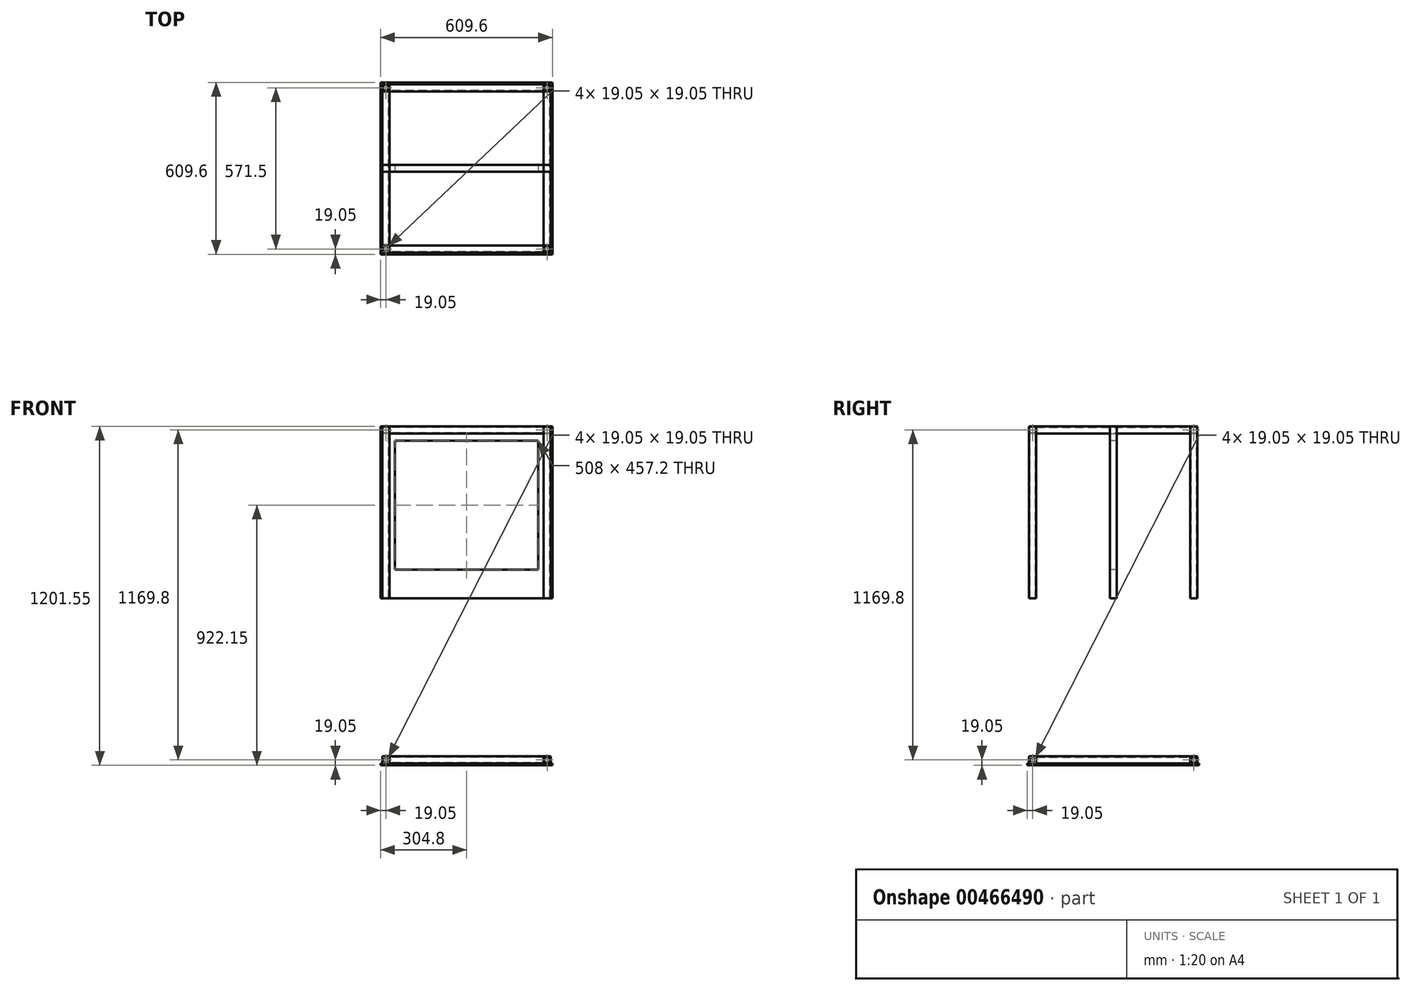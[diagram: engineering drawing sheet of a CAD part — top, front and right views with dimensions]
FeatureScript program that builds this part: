
annotation { "Feature Type Name" : "Feature", "Feature Type Description" : "" }
export const myFeature = defineFeature(function(context is Context, id is Id, definition is map)
    precondition{}
    {
        {
            assignVariable(context, id + "F0", {"name" : "OH", "anyValue" : 24});
        }
        {
            assignVariable(context, id + "F1", {"name" : "OD", "anyValue" : 24});
        }
        {
            var Q0;
            Q0=qCreatedBy(makeId("Front.planeOp"),FACE);
            var sketch = newSketch(context, id + "F2", { "sketchPlane" : qUnion([Q0])});
            skLineSegment(sketch, "E0.bottom", {"start": v(-304.8, 0) * mm, "end": v(304.8, 0) * mm});
            skLineSegment(sketch, "E0.top", {"start": v(-304.8, 609.6) * mm, "end": v(304.8, 609.6) * mm});
            skLineSegment(sketch, "E0.left", {"start": v(-304.8, 0) * mm, "end": v(-304.8, 609.6) * mm});
            skLineSegment(sketch, "E0.right", {"start": v(304.8, 0) * mm, "end": v(304.8, 609.6) * mm});
            skSolve(sketch);
        }
        {
            var Q0;
            Q0 = qSketchRegion(id + "F2", true);
            extrude(context, id + "F3", {"entities" : qUnion([Q0]), "depth" : (getVariable(context, 'OD') / 2) * mm, "hasSecondDirection" : true, "secondDirectionOppositeDirection" : true, "secondDirectionDepth" : (getVariable(context, 'OD') / 2) * mm});
        }
        {
            var Q0;
            Q0=makeQuery(id+"F3.opExtrude","CAP_FACE",FACE,{"disambiguationData":[OSD([sQuery(id+"F2.wireOp",EDGE,"E0.bottom"),sQuery(id+"F2.wireOp",EDGE,"E0.top"),sQuery(id+"F2.wireOp",EDGE,"E0.left"),sQuery(id+"F2.wireOp",EDGE,"E0.right")])],"isStart":false});
            var sketch = newSketch(context, id + "F4", { "sketchPlane" : qUnion([Q0])});
            skLineSegment(sketch, "E1.bottom", {"start": v(-254, 101.6) * mm, "end": v(254, 101.6) * mm});
            skLineSegment(sketch, "E1.top", {"start": v(-254, 558.8) * mm, "end": v(254, 558.8) * mm});
            skLineSegment(sketch, "E1.left", {"start": v(-254, 101.6) * mm, "end": v(-254, 558.8) * mm});
            skLineSegment(sketch, "E1.right", {"start": v(254, 101.6) * mm, "end": v(254, 558.8) * mm});
            skSolve(sketch);
        }
        {
            var Q0;
            Q0=makeQuery(id+"F3.opExtrude","SWEPT_FACE",FACE,{"disambiguationData":[OSD([sQuery(id+"F2.wireOp",EDGE,"E0.top")])]});
            var sketch = newSketch(context, id + "F5", { "sketchPlane" : qUnion([Q0])});
            skLineSegment(sketch, "E2.bottom", {"start": v(-298.45, 298.45) * mm, "end": v(298.45, 298.45) * mm});
            skLineSegment(sketch, "E2.top", {"start": v(-298.45, -298.45) * mm, "end": v(298.45, -298.45) * mm});
            skLineSegment(sketch, "E2.left", {"start": v(-298.45, 298.45) * mm, "end": v(-298.45, -298.45) * mm});
            skLineSegment(sketch, "E2.right", {"start": v(298.45, 298.45) * mm, "end": v(298.45, -298.45) * mm});
            skSolve(sketch);
        }
        {
            var Q0;
            Q0=makeQuery(id+"F5.imprint","IMPRINT",FACE,{"disambiguationData":[TD([[makeQuery(id+"F5.imprint","IMPRINT",EDGE,{"derivedFrom":sQuery(id+"F5.wireOp",EDGE,"E2.bottom")}),-1.0]])]});
            extrude(context, id + "F6", {"entities" : qUnion([Q0]), "operationType" : NewBodyOperationType.REMOVE, "endBound" : BoundingType.THROUGH_ALL, "oppositeDirection" : true, "depth" : 25.4 * mm});
        }
        {
            var Q0;
            Q0=makeQuery(id+"F4.imprint","IMPRINT",FACE,{"disambiguationData":[TD([[makeQuery(id+"F4.imprint","IMPRINT",EDGE,{"derivedFrom":sQuery(id+"F4.wireOp",EDGE,"E1.bottom")}),1.0]])]});
            extrude(context, id + "F7", {"entities" : qUnion([Q0]), "operationType" : NewBodyOperationType.REMOVE, "oppositeDirection" : true, "depth" : 25.4 * mm});
        }
        {
            var Q0;
            Q0=makeQuery(id+"F3.opExtrude","SWEPT_FACE",FACE,{"disambiguationData":[OSD([sQuery(id+"F2.wireOp",EDGE,"E0.top")])]});
            var sketch = newSketch(context, id + "F8", { "sketchPlane" : qUnion([Q0])});
            skLineSegment(sketch, "E3.bottom", {"start": v(-298.45, 298.45) * mm, "end": v(-273.05, 298.45) * mm});
            skLineSegment(sketch, "E3.top", {"start": v(-298.45, 273.05) * mm, "end": v(-273.05, 273.05) * mm});
            skLineSegment(sketch, "E3.left", {"start": v(-298.45, 298.45) * mm, "end": v(-298.45, 273.05) * mm});
            skLineSegment(sketch, "E3.right", {"start": v(-273.05, 298.45) * mm, "end": v(-273.05, 273.05) * mm});
            skLineSegment(sketch, "E4.bottom", {"start": v(-298.45, -298.45) * mm, "end": v(-273.05, -298.45) * mm});
            skLineSegment(sketch, "E4.top", {"start": v(-298.45, -273.05) * mm, "end": v(-273.05, -273.05) * mm});
            skLineSegment(sketch, "E4.left", {"start": v(-298.45, -298.45) * mm, "end": v(-298.45, -273.05) * mm});
            skLineSegment(sketch, "E4.right", {"start": v(-273.05, -298.45) * mm, "end": v(-273.05, -273.05) * mm});
            skLineSegment(sketch, "E5.bottom", {"start": v(298.45, 298.45) * mm, "end": v(273.05, 298.45) * mm});
            skLineSegment(sketch, "E5.top", {"start": v(298.45, 273.05) * mm, "end": v(273.05, 273.05) * mm});
            skLineSegment(sketch, "E5.left", {"start": v(298.45, 298.45) * mm, "end": v(298.45, 273.05) * mm});
            skLineSegment(sketch, "E5.right", {"start": v(273.05, 298.45) * mm, "end": v(273.05, 273.05) * mm});
            skLineSegment(sketch, "E6.bottom", {"start": v(298.45, -298.45) * mm, "end": v(273.05, -298.45) * mm});
            skLineSegment(sketch, "E6.top", {"start": v(298.45, -273.05) * mm, "end": v(273.05, -273.05) * mm});
            skLineSegment(sketch, "E6.left", {"start": v(298.45, -298.45) * mm, "end": v(298.45, -273.05) * mm});
            skLineSegment(sketch, "E6.right", {"start": v(273.05, -298.45) * mm, "end": v(273.05, -273.05) * mm});
            skLineSegment(sketch, "E7.bottom", {"start": v(276.22, -276.23) * mm, "end": v(295.27, -276.23) * mm});
            skLineSegment(sketch, "E7.top", {"start": v(276.22, -295.28) * mm, "end": v(295.27, -295.28) * mm});
            skLineSegment(sketch, "E7.left", {"start": v(276.22, -276.23) * mm, "end": v(276.22, -295.28) * mm});
            skLineSegment(sketch, "E7.right", {"start": v(295.27, -276.23) * mm, "end": v(295.27, -295.28) * mm});
            skLineSegment(sketch, "E8", {"start": v(-298.45, 0) * mm, "end": v(298.45, 0) * mm, "construction": true});
            skLineSegment(sketch, "E9", {"start": v(0, 298.45) * mm, "end": v(0, -298.45) * mm, "construction": true});
            skLineSegment(sketch, "E10.MirrorCS", {"start": v(276.22, 276.23) * mm, "end": v(295.27, 276.23) * mm});
            skLineSegment(sketch, "E11.MirrorCS", {"start": v(276.22, 276.23) * mm, "end": v(276.22, 295.28) * mm});
            skLineSegment(sketch, "E12.MirrorCS", {"start": v(276.22, 295.28) * mm, "end": v(295.27, 295.28) * mm});
            skLineSegment(sketch, "E13.MirrorCS", {"start": v(295.27, 276.23) * mm, "end": v(295.27, 295.28) * mm});
            skLineSegment(sketch, "E14.MirrorCS", {"start": v(-276.23, 295.28) * mm, "end": v(-295.28, 295.28) * mm});
            skLineSegment(sketch, "E15.MirrorCS", {"start": v(-295.28, 276.23) * mm, "end": v(-295.28, 295.28) * mm});
            skLineSegment(sketch, "E16.MirrorCS", {"start": v(-276.23, 276.23) * mm, "end": v(-276.23, 295.28) * mm});
            skLineSegment(sketch, "E17.MirrorCS", {"start": v(-276.23, 276.23) * mm, "end": v(-295.28, 276.23) * mm});
            skLineSegment(sketch, "E18.MirrorCS", {"start": v(-276.23, -276.23) * mm, "end": v(-295.28, -276.23) * mm});
            skLineSegment(sketch, "E19.MirrorCS", {"start": v(-295.28, -276.23) * mm, "end": v(-295.28, -295.28) * mm});
            skLineSegment(sketch, "E20.MirrorCS", {"start": v(-276.23, -276.23) * mm, "end": v(-276.23, -295.28) * mm});
            skLineSegment(sketch, "E21.MirrorCS", {"start": v(-276.23, -295.28) * mm, "end": v(-295.28, -295.28) * mm});
            skSolve(sketch);
        }
        {
            var Q0;
            Q0 = qSketchRegion(id + "F8", true);
            var Q1;
            Q1=makeQuery(id+"F3.opExtrude","SWEPT_FACE",FACE,{"disambiguationData":[OSD([sQuery(id+"F2.wireOp",EDGE,"E0.bottom")])]});
            extrude(context, id + "F9", {"entities" : qUnion([Q0]), "endBound" : BoundingType.UP_TO_SURFACE, "oppositeDirection" : true, "endBoundEntityFace" : qUnion([Q1]), "depth" : 25.4 * mm});
        }
        {
            var Q0;
            Q0=makeQuery(id+"F9.opExtrude","SWEPT_FACE",FACE,{"disambiguationData":[OSD([sQuery(id+"F8.wireOp",EDGE,"E3.right")])]});
            var sketch = newSketch(context, id + "F10", { "sketchPlane" : qUnion([Q0])});
            skLineSegment(sketch, "E22.bottom", {"start": v(298.45, 609.6) * mm, "end": v(273.05, 609.6) * mm});
            skLineSegment(sketch, "E22.top", {"start": v(298.45, 584.2) * mm, "end": v(273.05, 584.2) * mm});
            skLineSegment(sketch, "E22.left", {"start": v(298.45, 609.6) * mm, "end": v(298.45, 584.2) * mm});
            skLineSegment(sketch, "E22.right", {"start": v(273.05, 609.6) * mm, "end": v(273.05, 584.2) * mm});
            skLineSegment(sketch, "E23.bottom", {"start": v(295.28, 606.42) * mm, "end": v(276.23, 606.42) * mm});
            skLineSegment(sketch, "E23.top", {"start": v(295.28, 587.38) * mm, "end": v(276.23, 587.38) * mm});
            skLineSegment(sketch, "E23.left", {"start": v(295.28, 606.42) * mm, "end": v(295.28, 587.38) * mm});
            skLineSegment(sketch, "E23.right", {"start": v(276.23, 606.42) * mm, "end": v(276.23, 587.38) * mm});
            skSolve(sketch);
        }
        {
            var Q0;
            Q0 = qSketchRegion(id + "F10", true);
            var Q1;
            Q1=makeQuery(id+"F9.opExtrude","SWEPT_FACE",FACE,{"disambiguationData":[OSD([sQuery(id+"F8.wireOp",EDGE,"E5.right")])]});
            extrude(context, id + "F11", {"entities" : qUnion([Q0]), "endBound" : BoundingType.UP_TO_SURFACE, "endBoundEntityFace" : qUnion([Q1]), "depth" : 25.4 * mm});
        }
        {
            var Q0;
            Q0=makeQuery(id+"F11.opExtrude","SWEPT_BODY",BODY,{"disambiguationData":[OSD([sQuery(id+"F10.wireOp",EDGE,"E22.bottom"),sQuery(id+"F10.wireOp",EDGE,"E22.top"),sQuery(id+"F10.wireOp",EDGE,"E22.left"),sQuery(id+"F10.wireOp",EDGE,"E22.right"),sQuery(id+"F10.wireOp",EDGE,"E23.bottom"),sQuery(id+"F10.wireOp",EDGE,"E23.top"),sQuery(id+"F10.wireOp",EDGE,"E23.left"),sQuery(id+"F10.wireOp",EDGE,"E23.right")])]});
            var Q1;
            Q1=qCreatedBy(makeId("Front.planeOp"),FACE);
            mirror(context, id + "F12", {"entities" : qUnion([Q0]), "mirrorPlane" : qUnion([Q1])});
        }
        {
            var Q0;
            Q0=qCreatedBy(makeId("Top.planeOp"),FACE);
            cPlane(context, id + "F13", {"entities" : qUnion([Q0]), "cplaneType" : CPlaneType.OFFSET, "offset" : (getVariable(context, 'OH') / 2) * mm, "width" : 152.4 * mm, "height" : 152.4 * mm});
        }
        {
            var Q0;
            Q0=makeQuery(id+"F11.opExtrude","SWEPT_BODY",BODY,{"disambiguationData":[OSD([sQuery(id+"F10.wireOp",EDGE,"E22.bottom"),sQuery(id+"F10.wireOp",EDGE,"E22.top"),sQuery(id+"F10.wireOp",EDGE,"E22.left"),sQuery(id+"F10.wireOp",EDGE,"E22.right"),sQuery(id+"F10.wireOp",EDGE,"E23.bottom"),sQuery(id+"F10.wireOp",EDGE,"E23.top"),sQuery(id+"F10.wireOp",EDGE,"E23.left"),sQuery(id+"F10.wireOp",EDGE,"E23.right")])]});
            var Q1;
            Q1=makeQuery(id+"F12.opPattern","COPY",BODY,{"derivedFrom":makeQuery(id+"F11.opExtrude","SWEPT_BODY",BODY,{"disambiguationData":[OSD([sQuery(id+"F10.wireOp",EDGE,"E22.bottom"),sQuery(id+"F10.wireOp",EDGE,"E22.top"),sQuery(id+"F10.wireOp",EDGE,"E22.left"),sQuery(id+"F10.wireOp",EDGE,"E22.right"),sQuery(id+"F10.wireOp",EDGE,"E23.bottom"),sQuery(id+"F10.wireOp",EDGE,"E23.top"),sQuery(id+"F10.wireOp",EDGE,"E23.left"),sQuery(id+"F10.wireOp",EDGE,"E23.right")])]}),"instanceName":"1"});
            var Q2;
            Q2=qCreatedBy(id+"F13.planeOp",FACE);
            mirror(context, id + "F14", {"entities" : qUnion([Q0, Q1]), "mirrorPlane" : qUnion([Q2])});
        }
        {
            var Q0;
            Q0=makeQuery(id+"F9.opExtrude","SWEPT_FACE",FACE,{"disambiguationData":[OSD([sQuery(id+"F8.wireOp",EDGE,"E5.top")])]});
            var sketch = newSketch(context, id + "F15", { "sketchPlane" : qUnion([Q0])});
            skLineSegment(sketch, "E24.bottom", {"start": v(298.45, 609.6) * mm, "end": v(273.05, 609.6) * mm});
            skLineSegment(sketch, "E24.top", {"start": v(298.45, 584.2) * mm, "end": v(273.05, 584.2) * mm});
            skLineSegment(sketch, "E24.left", {"start": v(298.45, 609.6) * mm, "end": v(298.45, 584.2) * mm});
            skLineSegment(sketch, "E24.right", {"start": v(273.05, 609.6) * mm, "end": v(273.05, 584.2) * mm});
            skLineSegment(sketch, "E25.0", {"start": v(295.27, 587.38) * mm, "end": v(276.23, 587.38) * mm});
            skLineSegment(sketch, "E25.1", {"start": v(295.27, 606.42) * mm, "end": v(295.27, 587.38) * mm});
            skLineSegment(sketch, "E25.2", {"start": v(295.27, 606.42) * mm, "end": v(276.23, 606.42) * mm});
            skLineSegment(sketch, "E25.3", {"start": v(276.23, 606.42) * mm, "end": v(276.23, 587.38) * mm});
            skSolve(sketch);
        }
        {
            var Q0;
            Q0 = qSketchRegion(id + "F15", true);
            var Q1;
            Q1=makeQuery(id+"F9.opExtrude","SWEPT_FACE",FACE,{"disambiguationData":[OSD([sQuery(id+"F8.wireOp",EDGE,"E6.top")])]});
            extrude(context, id + "F16", {"entities" : qUnion([Q0]), "endBound" : BoundingType.UP_TO_SURFACE, "endBoundEntityFace" : qUnion([Q1]), "depth" : 25.4 * mm});
        }
        {
            var Q0;
            Q0=makeQuery(id+"F16.opExtrude","SWEPT_BODY",BODY,{"disambiguationData":[OSD([sQuery(id+"F15.wireOp",EDGE,"E24.bottom"),sQuery(id+"F15.wireOp",EDGE,"E24.top"),sQuery(id+"F15.wireOp",EDGE,"E24.left"),sQuery(id+"F15.wireOp",EDGE,"E24.right"),sQuery(id+"F15.wireOp",EDGE,"E25.0"),sQuery(id+"F15.wireOp",EDGE,"E25.1"),sQuery(id+"F15.wireOp",EDGE,"E25.2"),sQuery(id+"F15.wireOp",EDGE,"E25.3")])]});
            var Q1;
            Q1=qCreatedBy(makeId("Right.planeOp"),FACE);
            mirror(context, id + "F17", {"entities" : qUnion([Q0]), "mirrorPlane" : qUnion([Q1])});
        }
        {
            var Q0;
            Q0=makeQuery(id+"F16.opExtrude","SWEPT_BODY",BODY,{"disambiguationData":[OSD([sQuery(id+"F15.wireOp",EDGE,"E24.bottom"),sQuery(id+"F15.wireOp",EDGE,"E24.top"),sQuery(id+"F15.wireOp",EDGE,"E24.left"),sQuery(id+"F15.wireOp",EDGE,"E24.right"),sQuery(id+"F15.wireOp",EDGE,"E25.0"),sQuery(id+"F15.wireOp",EDGE,"E25.1"),sQuery(id+"F15.wireOp",EDGE,"E25.2"),sQuery(id+"F15.wireOp",EDGE,"E25.3")])]});
            var Q1;
            Q1=makeQuery(id+"F17.opPattern","COPY",BODY,{"derivedFrom":makeQuery(id+"F16.opExtrude","SWEPT_BODY",BODY,{"disambiguationData":[OSD([sQuery(id+"F15.wireOp",EDGE,"E24.bottom"),sQuery(id+"F15.wireOp",EDGE,"E24.top"),sQuery(id+"F15.wireOp",EDGE,"E24.left"),sQuery(id+"F15.wireOp",EDGE,"E24.right"),sQuery(id+"F15.wireOp",EDGE,"E25.0"),sQuery(id+"F15.wireOp",EDGE,"E25.1"),sQuery(id+"F15.wireOp",EDGE,"E25.2"),sQuery(id+"F15.wireOp",EDGE,"E25.3")])]}),"instanceName":"1"});
            var Q2;
            Q2=qCreatedBy(id+"F13.planeOp",FACE);
            mirror(context, id + "F18", {"entities" : qUnion([Q0, Q1]), "mirrorPlane" : qUnion([Q2])});
        }
        {
            var Q0;
            Q0=makeQuery(id+"F14.opPattern","COPY",FACE,{"derivedFrom":makeQuery(id+"F12.opPattern","COPY",FACE,{"derivedFrom":makeQuery(id+"F11.opExtrude","SWEPT_FACE",FACE,{"disambiguationData":[OSD([sQuery(id+"F10.wireOp",EDGE,"E22.bottom")])]}),"instanceName":"1"}),"instanceName":"1"});
            var sketch = newSketch(context, id + "F19", { "sketchPlane" : qUnion([Q0])});
            skLineSegment(sketch, "E26.bottom", {"start": v(304.8, 304.8) * mm, "end": v(-304.8, 304.8) * mm});
            skLineSegment(sketch, "E26.top", {"start": v(304.8, -304.8) * mm, "end": v(-304.8, -304.8) * mm});
            skLineSegment(sketch, "E26.left", {"start": v(304.8, 304.8) * mm, "end": v(304.8, -304.8) * mm});
            skLineSegment(sketch, "E26.right", {"start": v(-304.8, 304.8) * mm, "end": v(-304.8, -304.8) * mm});
            skSolve(sketch);
        }
        {
            var Q0;
            Q0 = qSketchRegion(id + "F19", true);
            extrude(context, id + "F20", {"entities" : qUnion([Q0]), "depth" : 6.35 * mm});
        }
    });
